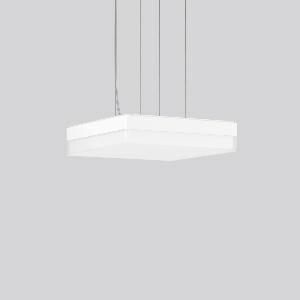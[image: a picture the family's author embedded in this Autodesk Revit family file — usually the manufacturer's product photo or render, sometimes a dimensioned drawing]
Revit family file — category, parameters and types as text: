
# Revit family: flat_slim_square_312541_002_730_d66b
name_source: partatom
category: Lighting Fixtures
units: mm (PartAtom-declared; Revit-internal decimal feet)

## family parameters
Cut with Voids When Loaded = No
Host = Face
Light Source = No
Part Type = Normal
Room Calculation Point = No
Round Connector Dimension = Use Diameter
Shared = No

## types (1)
- MultiLumen 2 840 (1 x LED Modul 840, 2400 lm, 4000)
    Apparent Load = 21 VA
    CIE Flux Codes = 43 74 93 92 100
    Color Rendering = 80
    Color Temperature = 4000
    Default Elevation = 1800 mm
    Height = 70 mm
    Lamp = 1 x LED Modul 840
    Lamp Light Flux = 2400 lm
    Lamp count = 1
    Length = 300 mm
    Lifetime = 50000 h
    Luminous efficacy = 114 lm/W
    Manufacturer = RZB
    ModVariant = No
    Model = 312541.002.730
    Mounting Place = Ceiling
    Mounting Type = Pendant
    Number of Poles = 1
    OnlyDefault = Yes
    Power Factor = 1
    Product Name = FLAT SLIM square
    Product group = Pendant luminaires
    ProductGroupID = 902
    Protection Class = Protection class I
    Protection Degree = IP 40
    RLX_Detail_Level = 1
    RLX_Emergency_Light_Flux = 0 lm
    RLX_Emergency_Type = 0
    RLX_Emergency_Type_DB = No
    RlxData = <blob elided: 14441 chars, md5=867f8373>
    Socket = socket
    Standby Power = 0 W
    System Light Flux = 2400 lm
    System Power = 21 W
    Type Comments = MultiLumen 2 840
    Type Image = 312541.002.jpg
    URL = http://relux.com
    VarID = multilumen_2_840
    Voltage = 230 V
    Voltage Range = 220-240 V
    Weight = 0.00 kg
    Width = 300 mm

## geometry (parser evidence)
native form markers: Sweep x16
no freeform markers — native parametric forms only
